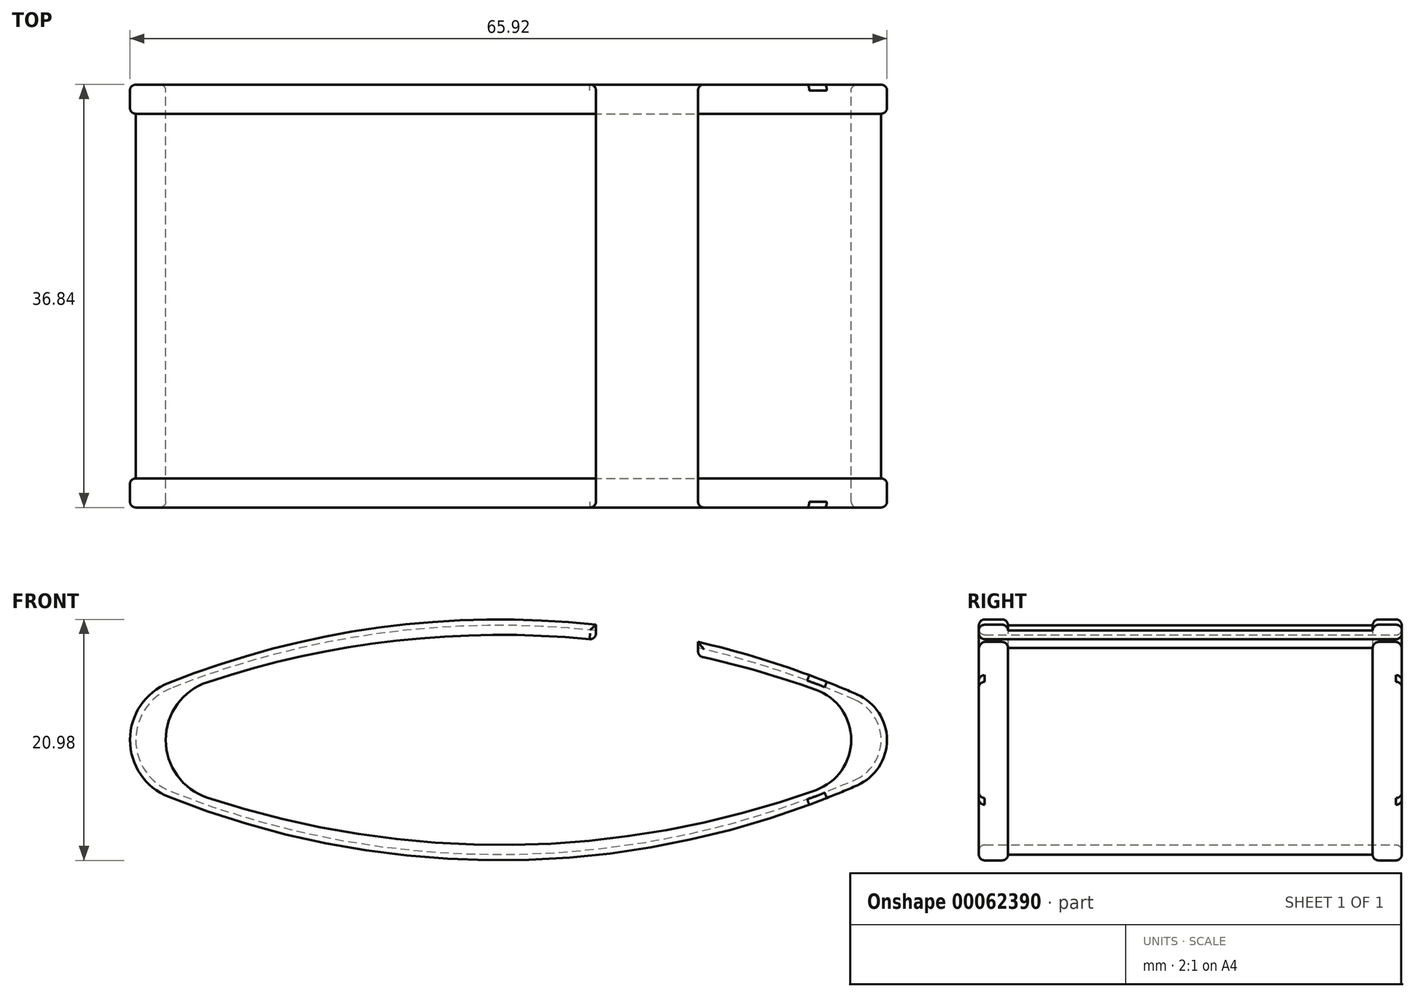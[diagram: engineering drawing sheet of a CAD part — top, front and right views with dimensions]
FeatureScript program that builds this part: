
annotation { "Feature Type Name" : "Feature", "Feature Type Description" : "" }
export const myFeature = defineFeature(function(context is Context, id is Id, definition is map)
    precondition{}
    {
        {
            var Q0;
            Q0=qCreatedBy(makeId("Front.planeOp"),FACE);
            var sketch = newSketch(context, id + "F0", { "sketchPlane" : qUnion([Q0])});
            skLineSegment(sketch, "E0", {"start": v(-32.45, 0) * mm, "end": v(32.45, 0) * mm, "construction": true});
            skLineSegment(sketch, "E1", {"start": v(0, 9.98) * mm, "end": v(0, -9.98) * mm, "construction": true});
            skPoint(sketch, "E2", {"position": v(0, 0) * mm});
            skEllipse(sketch, "E3", {"center": v(0, 0) * mm, "majorRadius": 9.98 * mm, "minorRadius": 32.45 * mm, "majorAxis": v(0, 1), "construction": true});
            skArc(sketch, "E4", {"start": v(30.17, -3.49) * mm, "mid": v(32.45, 0) * mm, "end": v(30.17, 3.49) * mm});
            skArc(sketch, "E5", {"start": v(-29.41, 4.48) * mm, "mid": v(-32.45, 0) * mm, "end": v(-29.41, -4.48) * mm});
            skArc(sketch, "E6", {"start": v(-29.41, 4.48) * mm, "mid": v(0.48, 9.97) * mm, "end": v(30.17, 3.49) * mm});
            skArc(sketch, "E7", {"start": v(30.17, -3.49) * mm, "mid": v(0.48, -9.97) * mm, "end": v(-29.41, -4.48) * mm});
            skSolve(sketch);
        }
        {
            var Q0;
            Q0=makeQuery(id+"F0.imprint","IMPRINT",FACE,{"disambiguationData":[TD([[makeQuery(id+"F0.imprint","IMPRINT",EDGE,{"derivedFrom":sQuery(id+"F0.wireOp",EDGE,"E3")}),1.0]])]});
            var Q1;
            Q1=makeQuery(id+"F0.imprint","IMPRINT",FACE,{"disambiguationData":[TD([[makeQuery(id+"F0.imprint","IMPRINT",EDGE,{"derivedFrom":sQuery(id+"F0.wireOp",EDGE,"E4")}),1.0]])]});
            extrude(context, id + "F1", {"entities" : qUnion([Q0, Q1]), "depth" : 15.88 * mm});
        }
        {
            var Q0;
            Q0=makeQuery(id+"F1.opExtrude","CAP_FACE",FACE,{"disambiguationData":[OSD([sQuery(id+"F0.wireOp",EDGE,"E4"),sQuery(id+"F0.wireOp",EDGE,"E5"),sQuery(id+"F0.wireOp",EDGE,"E6"),sQuery(id+"F0.wireOp",EDGE,"E7")])],"isStart":false});
            var sketch = newSketch(context, id + "F2", { "sketchPlane" : qUnion([Q0])});
            skArc(sketch, "E8.0", {"start": v(-29.6, 4.95) * mm, "mid": v(0.49, 10.48) * mm, "end": v(30.37, 3.95) * mm});
            skArc(sketch, "E8.1", {"start": v(-29.6, 4.95) * mm, "mid": v(-32.96, 0) * mm, "end": v(-29.6, -4.95) * mm});
            skArc(sketch, "E8.2", {"start": v(30.37, -3.95) * mm, "mid": v(0.49, -10.48) * mm, "end": v(-29.6, -4.95) * mm});
            skArc(sketch, "E8.3", {"start": v(30.37, -3.95) * mm, "mid": v(32.96, 0) * mm, "end": v(30.37, 3.95) * mm});
            skSolve(sketch);
        }
        {
            var Q0;
            Q0 = qSketchRegion(id + "F2", true);
            extrude(context, id + "F3", {"entities" : qUnion([Q0]), "operationType" : NewBodyOperationType.ADD, "depth" : 2.54 * mm});
        }
        {
            var Q0;
            Q0=makeQuery(id+"F1.opExtrude","CAP_FACE",FACE,{"disambiguationData":[OSD([sQuery(id+"F0.wireOp",EDGE,"E4"),sQuery(id+"F0.wireOp",EDGE,"E5"),sQuery(id+"F0.wireOp",EDGE,"E6"),sQuery(id+"F0.wireOp",EDGE,"E7")])],"isStart":true});
            var sketch = newSketch(context, id + "F4", { "sketchPlane" : qUnion([Q0])});
            skLineSegment(sketch, "E9.bottom", {"start": v(-3.24, 2.21) * mm, "end": v(11.05, 2.21) * mm, "construction": true});
            skLineSegment(sketch, "E9.top", {"start": v(-3.24, -2.28) * mm, "end": v(11.05, -2.28) * mm, "construction": true});
            skLineSegment(sketch, "E9.left", {"start": v(-3.24, 2.21) * mm, "end": v(-3.24, -2.28) * mm, "construction": true});
            skLineSegment(sketch, "E9.right", {"start": v(14.5, 2.21) * mm, "end": v(14.5, -2.28) * mm, "construction": true});
            skLineSegment(sketch, "E10", {"start": v(14.5, -0.03) * mm, "end": v(11.05, 4.42) * mm, "construction": true});
            skLineSegment(sketch, "E11", {"start": v(11.05, 4.42) * mm, "end": v(11.05, 2.21) * mm, "construction": true});
            skLineSegment(sketch, "E12", {"start": v(11.05, -4.53) * mm, "end": v(14.5, -0.03) * mm, "construction": true});
            skLineSegment(sketch, "E13.trimOffspring", {"start": v(11.05, -2.28) * mm, "end": v(11.05, -4.53) * mm, "construction": true});
            skSolve(sketch);
        }
        {
            var Q0;
            Q0=makeQuery(id+"F4.imprint","IMPRINT",FACE,{"disambiguationData":[TD([[makeQuery(id+"F4.imprint","IMPRINT",EDGE,{"derivedFrom":makeQuery(id+"F1.opExtrude","CAP_EDGE",EDGE,{"disambiguationData":[OSD([sQuery(id+"F0.wireOp",EDGE,"E4")])],"isStart":true})}),-1.0]])]});
            var sketch = newSketch(context, id + "F5", { "sketchPlane" : qUnion([Q0])});
            skArc(sketch, "E14.0", {"start": v(-26.78, 4.36) * mm, "mid": v(-29.84, 0) * mm, "end": v(-26.78, -4.36) * mm});
            skArc(sketch, "E14.1", {"start": v(26.2, 5.03) * mm, "mid": v(-0.34, 9.14) * mm, "end": v(-26.78, 4.36) * mm});
            skArc(sketch, "E14.2", {"start": v(26.2, -5.03) * mm, "mid": v(29.85, 0) * mm, "end": v(26.2, 5.03) * mm});
            skArc(sketch, "E14.3", {"start": v(-26.78, -4.36) * mm, "mid": v(-0.34, -9.14) * mm, "end": v(26.2, -5.03) * mm});
            skLineSegment(sketch, "E15", {"start": v(-29.85, 0) * mm, "end": v(29.85, 0) * mm, "construction": true});
            skLineSegment(sketch, "E16", {"start": v(0, -9.14) * mm, "end": v(0, 9.14) * mm, "construction": true});
            skPoint(sketch, "E17", {"position": v(0, 0) * mm});
            skSolve(sketch);
        }
        {
            var Q0;
            Q0 = qSketchRegion(id + "F5", true);
            extrude(context, id + "F6", {"entities" : qUnion([Q0]), "operationType" : NewBodyOperationType.REMOVE, "endBound" : BoundingType.THROUGH_ALL, "oppositeDirection" : true, "depth" : 25.4 * mm});
        }
        {
            var Q0;
            Q0=makeQuery(id+"F3.opExtrude","CAP_FACE",FACE,{"disambiguationData":[OSD([sQuery(id+"F2.wireOp",EDGE,"E8.0"),sQuery(id+"F2.wireOp",EDGE,"E8.1"),sQuery(id+"F2.wireOp",EDGE,"E8.2"),sQuery(id+"F2.wireOp",EDGE,"E8.3")])],"isStart":false});
            var sketch = newSketch(context, id + "F7", { "sketchPlane" : qUnion([Q0])});
            skLineSegment(sketch, "E18.bottom", {"start": v(7.62, 15.6) * mm, "end": v(16.5, 15.6) * mm});
            skLineSegment(sketch, "E18.top", {"start": v(7.62, -2.82) * mm, "end": v(16.5, -2.82) * mm});
            skLineSegment(sketch, "E18.left", {"start": v(7.62, 15.6) * mm, "end": v(7.62, -2.82) * mm});
            skLineSegment(sketch, "E18.right", {"start": v(16.5, 15.6) * mm, "end": v(16.5, -2.82) * mm});
            skSolve(sketch);
        }
        {
            var Q0;
            Q0 = qSketchRegion(id + "F7", true);
            extrude(context, id + "F8", {"entities" : qUnion([Q0]), "operationType" : NewBodyOperationType.REMOVE, "endBound" : BoundingType.THROUGH_ALL, "oppositeDirection" : true, "depth" : 25.4 * mm});
        }
        {
            var Q0;
            {var subQ0=makeQuery(id+"F3.opExtrude","CAP_FACE",FACE,{"disambiguationData":[OSD([sQuery(id+"F2.wireOp",EDGE,"E8.0"),sQuery(id+"F2.wireOp",EDGE,"E8.1"),sQuery(id+"F2.wireOp",EDGE,"E8.2"),sQuery(id+"F2.wireOp",EDGE,"E8.3")])],"isStart":false});var subQ1=makeQuery(id+"F6.opExtrude","SWEPT_FACE",FACE,{"disambiguationData":[OSD([sQuery(id+"F5.wireOp",EDGE,"E14.1")])]});Q0=makeQuery(id+"F8.boolean.opBoolean","SPLIT",EDGE,{"disambiguationData":[TD([makeQuery(id+"F6.boolean.opBoolean","COPY",FACE,{"derivedFrom":makeQuery(id+"F6.opExtrude","SWEPT_FACE",FACE,{"disambiguationData":[OSD([sQuery(id+"F5.wireOp",EDGE,"E14.2")])]})})])],"derivedFrom":makeQuery(id+"F6.boolean.opBoolean","INTERSECT",EDGE,{"derivedFrom":[subQ0,subQ1]})});}
            fillet(context, id + "F9", {"entities" : qUnion([Q0]), "radius" : 0.5 * mm, "tangentPropagation" : true, "allowEdgeOverflow" : false});
        }
        {
            var Q0;
            Q0=makeQuery(id+"F8.boolean.opBoolean","INTERSECT",EDGE,{"derivedFrom":[makeQuery(id+"F6.boolean.opBoolean","COPY",FACE,{"derivedFrom":makeQuery(id+"F6.opExtrude","SWEPT_FACE",FACE,{"disambiguationData":[OSD([sQuery(id+"F5.wireOp",EDGE,"E14.1")])]})}),makeQuery(id+"F8.opExtrude","SWEPT_FACE",FACE,{"disambiguationData":[OSD([sQuery(id+"F7.wireOp",EDGE,"E18.left")])]})]});
            var Q1;
            Q1=makeQuery(id+"F8.boolean.opBoolean","INTERSECT",EDGE,{"derivedFrom":[makeQuery(id+"F6.boolean.opBoolean","COPY",FACE,{"derivedFrom":makeQuery(id+"F6.opExtrude","SWEPT_FACE",FACE,{"disambiguationData":[OSD([sQuery(id+"F5.wireOp",EDGE,"E14.1")])]})}),makeQuery(id+"F8.opExtrude","SWEPT_FACE",FACE,{"disambiguationData":[OSD([sQuery(id+"F7.wireOp",EDGE,"E18.right")])]})]});
            var Q2;
            {var subQ0=sQuery(id+"F2.wireOp",EDGE,"E8.0");var subQ1=sQuery(id+"F2.wireOp",EDGE,"E8.1");Q2=makeQuery(id+"F8.boolean.opBoolean","SPLIT",EDGE,{"disambiguationData":[TD([makeQuery(id+"F3.opExtrude","SWEPT_FACE",FACE,{"disambiguationData":[OSD([subQ1])]})])],"derivedFrom":makeQuery(id+"F3.opExtrude","CAP_EDGE",EDGE,{"disambiguationData":[OSD([subQ0])],"isStart":false})});}
            var Q3;
            {var subQ0=sQuery(id+"F2.wireOp",EDGE,"E8.0");var subQ1=sQuery(id+"F2.wireOp",EDGE,"E8.1");Q3=makeQuery(id+"F8.boolean.opBoolean","SPLIT",EDGE,{"disambiguationData":[TD([makeQuery(id+"F3.opExtrude","SWEPT_FACE",FACE,{"disambiguationData":[OSD([subQ1])]})])],"derivedFrom":makeQuery(id+"F3.opExtrude","CAP_EDGE",EDGE,{"disambiguationData":[OSD([subQ0])],"isStart":true})});}
            fillet(context, id + "F10", {"entities" : qUnion([Q0, Q1, Q2, Q3]), "radius" : 0.5 * mm, "tangentPropagation" : true, "allowEdgeOverflow" : false});
        }
        {
            var Q0;
            Q0=makeQuery(id+"F1.opExtrude","SWEPT_BODY",BODY,{"disambiguationData":[OSD([sQuery(id+"F0.wireOp",EDGE,"E4"),sQuery(id+"F0.wireOp",EDGE,"E5"),sQuery(id+"F0.wireOp",EDGE,"E6"),sQuery(id+"F0.wireOp",EDGE,"E7")])]});
            var Q1;
            Q1=makeQuery(id+"F4.imprint","IMPRINT",FACE,{"disambiguationData":[TD([[makeQuery(id+"F4.imprint","IMPRINT",EDGE,{"derivedFrom":makeQuery(id+"F1.opExtrude","CAP_EDGE",EDGE,{"disambiguationData":[OSD([sQuery(id+"F0.wireOp",EDGE,"E4")])],"isStart":true})}),-1.0]])]});
            mirror(context, id + "F11", {"operationType" : NewBodyOperationType.ADD, "entities" : qUnion([Q0]), "mirrorPlane" : qUnion([Q1])});
        }
    });
